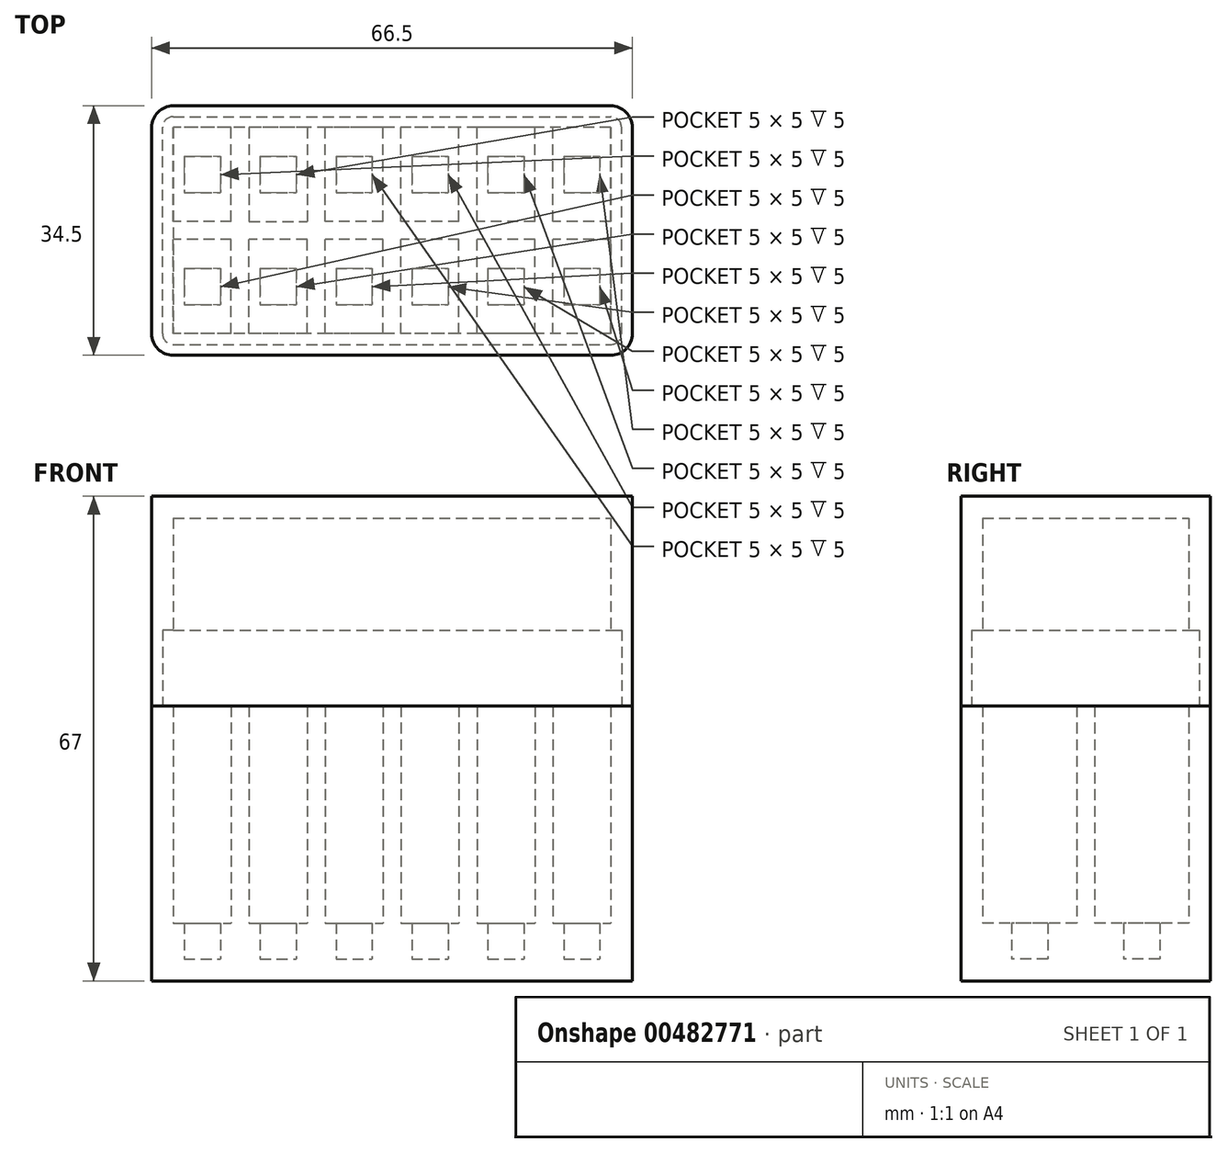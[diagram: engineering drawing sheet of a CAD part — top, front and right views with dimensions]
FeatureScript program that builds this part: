
annotation { "Feature Type Name" : "Feature", "Feature Type Description" : "" }
export const myFeature = defineFeature(function(context is Context, id is Id, definition is map)
    precondition{}
    {
        {
            var Q0;
            Q0=qCreatedBy(makeId("Top.planeOp"),FACE);
            var sketch = newSketch(context, id + "F0", { "sketchPlane" : qUnion([Q0])});
            skLineSegment(sketch, "E0.bottom", {"start": v(3, 0) * mm, "end": v(63.5, 0) * mm});
            skLineSegment(sketch, "E0.top", {"start": v(3, 34.5) * mm, "end": v(63.5, 34.5) * mm});
            skLineSegment(sketch, "E0.left", {"start": v(0, 3) * mm, "end": v(0, 31.5) * mm});
            skLineSegment(sketch, "E0.right", {"start": v(66.5, 3) * mm, "end": v(66.5, 31.5) * mm});
            skPoint(sketch, "E1.visualSharp", {"position": v(0, 34.5) * mm});
            skArc(sketch, "E1.filletArc", {"start": v(3, 34.5) * mm, "mid": v(0.88, 33.62) * mm, "end": v(0, 31.5) * mm});
            skPoint(sketch, "E2.visualSharp", {"position": v(66.5, 34.5) * mm});
            skArc(sketch, "E2.filletArc", {"start": v(66.5, 31.5) * mm, "mid": v(65.62, 33.62) * mm, "end": v(63.5, 34.5) * mm});
            skPoint(sketch, "E3.visualSharp", {"position": v(66.5, 0) * mm});
            skArc(sketch, "E3.filletArc", {"start": v(63.5, 0) * mm, "mid": v(65.62, 0.88) * mm, "end": v(66.5, 3) * mm});
            skPoint(sketch, "E4.visualSharp", {"position": v(0, 0) * mm});
            skArc(sketch, "E4.filletArc", {"start": v(0, 3) * mm, "mid": v(0.88, 0.88) * mm, "end": v(3, 0) * mm});
            skSolve(sketch);
        }
        {
            var Q0;
            Q0 = qSketchRegion(id + "F0", true);
            extrude(context, id + "F1", {"entities" : qUnion([Q0]), "depth" : 3 * mm});
        }
        {
            var Q0;
            Q0=makeQuery(id+"F1.opExtrude","CAP_FACE",FACE,{"disambiguationData":[OSD([sQuery(id+"F0.wireOp",EDGE,"E0.bottom"),sQuery(id+"F0.wireOp",EDGE,"E0.top"),sQuery(id+"F0.wireOp",EDGE,"E0.left"),sQuery(id+"F0.wireOp",EDGE,"E0.right"),sQuery(id+"F0.wireOp",EDGE,"E1.filletArc"),sQuery(id+"F0.wireOp",EDGE,"E2.filletArc"),sQuery(id+"F0.wireOp",EDGE,"E3.filletArc"),sQuery(id+"F0.wireOp",EDGE,"E4.filletArc")])],"isStart":false});
            var sketch = newSketch(context, id + "F2", { "sketchPlane" : qUnion([Q0])});
            skArc(sketch, "E5.0", {"start": v(63.5, 0) * mm, "mid": v(65.62, 0.88) * mm, "end": v(66.5, 3) * mm});
            skLineSegment(sketch, "E5.1", {"start": v(3, 34.5) * mm, "end": v(63.5, 34.5) * mm});
            skArc(sketch, "E5.2", {"start": v(66.5, 31.5) * mm, "mid": v(65.62, 33.62) * mm, "end": v(63.5, 34.5) * mm});
            skLineSegment(sketch, "E5.3", {"start": v(3, 0) * mm, "end": v(63.5, 0) * mm});
            skArc(sketch, "E5.4", {"start": v(3, 34.5) * mm, "mid": v(0.88, 33.62) * mm, "end": v(0, 31.5) * mm});
            skLineSegment(sketch, "E5.5", {"start": v(66.5, 3) * mm, "end": v(66.5, 31.5) * mm});
            skArc(sketch, "E5.6", {"start": v(0, 3) * mm, "mid": v(0.88, 0.88) * mm, "end": v(3, 0) * mm});
            skLineSegment(sketch, "E5.7", {"start": v(0, 3) * mm, "end": v(0, 31.5) * mm});
            skLineSegment(sketch, "E6.bottom", {"start": v(4.5, 12) * mm, "end": v(9.5, 12) * mm});
            skLineSegment(sketch, "E6.top", {"start": v(4.5, 7) * mm, "end": v(9.5, 7) * mm});
            skLineSegment(sketch, "E6.left", {"start": v(4.5, 12) * mm, "end": v(4.5, 7) * mm});
            skLineSegment(sketch, "E6.right", {"start": v(9.5, 12) * mm, "end": v(9.5, 7) * mm});
            skLineSegment(sketch, "E7.0.1.0", {"start": v(4.5, 22.5) * mm, "end": v(9.5, 22.5) * mm});
            skLineSegment(sketch, "E7.0.1.1", {"start": v(9.5, 27.5) * mm, "end": v(9.5, 22.5) * mm});
            skLineSegment(sketch, "E7.0.1.2", {"start": v(4.5, 27.5) * mm, "end": v(4.5, 22.5) * mm});
            skLineSegment(sketch, "E7.0.1.3", {"start": v(4.5, 27.5) * mm, "end": v(9.5, 27.5) * mm});
            skLineSegment(sketch, "E7.1.0.0", {"start": v(15, 7) * mm, "end": v(20, 7) * mm});
            skLineSegment(sketch, "E7.1.0.1", {"start": v(20, 12) * mm, "end": v(20, 7) * mm});
            skLineSegment(sketch, "E7.1.0.2", {"start": v(15, 12) * mm, "end": v(15, 7) * mm});
            skLineSegment(sketch, "E7.1.0.3", {"start": v(15, 12) * mm, "end": v(20, 12) * mm});
            skLineSegment(sketch, "E7.1.1.0", {"start": v(15, 22.5) * mm, "end": v(20, 22.5) * mm});
            skLineSegment(sketch, "E7.1.1.1", {"start": v(20, 27.5) * mm, "end": v(20, 22.5) * mm});
            skLineSegment(sketch, "E7.1.1.2", {"start": v(15, 27.5) * mm, "end": v(15, 22.5) * mm});
            skLineSegment(sketch, "E7.1.1.3", {"start": v(15, 27.5) * mm, "end": v(20, 27.5) * mm});
            skLineSegment(sketch, "E7.2.0.0", {"start": v(25.5, 7) * mm, "end": v(30.5, 7) * mm});
            skLineSegment(sketch, "E7.2.0.1", {"start": v(30.5, 12) * mm, "end": v(30.5, 7) * mm});
            skLineSegment(sketch, "E7.2.0.2", {"start": v(25.5, 12) * mm, "end": v(25.5, 7) * mm});
            skLineSegment(sketch, "E7.2.0.3", {"start": v(25.5, 12) * mm, "end": v(30.5, 12) * mm});
            skLineSegment(sketch, "E7.2.1.0", {"start": v(25.5, 22.5) * mm, "end": v(30.5, 22.5) * mm});
            skLineSegment(sketch, "E7.2.1.1", {"start": v(30.5, 27.5) * mm, "end": v(30.5, 22.5) * mm});
            skLineSegment(sketch, "E7.2.1.2", {"start": v(25.5, 27.5) * mm, "end": v(25.5, 22.5) * mm});
            skLineSegment(sketch, "E7.2.1.3", {"start": v(25.5, 27.5) * mm, "end": v(30.5, 27.5) * mm});
            skLineSegment(sketch, "E7.3.0.0", {"start": v(36, 7) * mm, "end": v(41, 7) * mm});
            skLineSegment(sketch, "E7.3.0.1", {"start": v(41, 12) * mm, "end": v(41, 7) * mm});
            skLineSegment(sketch, "E7.3.0.2", {"start": v(36, 12) * mm, "end": v(36, 7) * mm});
            skLineSegment(sketch, "E7.3.0.3", {"start": v(36, 12) * mm, "end": v(41, 12) * mm});
            skLineSegment(sketch, "E7.3.1.0", {"start": v(36, 22.5) * mm, "end": v(41, 22.5) * mm});
            skLineSegment(sketch, "E7.3.1.1", {"start": v(41, 27.5) * mm, "end": v(41, 22.5) * mm});
            skLineSegment(sketch, "E7.3.1.2", {"start": v(36, 27.5) * mm, "end": v(36, 22.5) * mm});
            skLineSegment(sketch, "E7.3.1.3", {"start": v(36, 27.5) * mm, "end": v(41, 27.5) * mm});
            skLineSegment(sketch, "E7.4.0.0", {"start": v(46.5, 7) * mm, "end": v(51.5, 7) * mm});
            skLineSegment(sketch, "E7.4.0.1", {"start": v(51.5, 12) * mm, "end": v(51.5, 7) * mm});
            skLineSegment(sketch, "E7.4.0.2", {"start": v(46.5, 12) * mm, "end": v(46.5, 7) * mm});
            skLineSegment(sketch, "E7.4.0.3", {"start": v(46.5, 12) * mm, "end": v(51.5, 12) * mm});
            skLineSegment(sketch, "E7.4.1.0", {"start": v(46.5, 22.5) * mm, "end": v(51.5, 22.5) * mm});
            skLineSegment(sketch, "E7.4.1.1", {"start": v(51.5, 27.5) * mm, "end": v(51.5, 22.5) * mm});
            skLineSegment(sketch, "E7.4.1.2", {"start": v(46.5, 27.5) * mm, "end": v(46.5, 22.5) * mm});
            skLineSegment(sketch, "E7.4.1.3", {"start": v(46.5, 27.5) * mm, "end": v(51.5, 27.5) * mm});
            skLineSegment(sketch, "E7.5.0.0", {"start": v(57, 7) * mm, "end": v(62, 7) * mm});
            skLineSegment(sketch, "E7.5.0.1", {"start": v(62, 12) * mm, "end": v(62, 7) * mm});
            skLineSegment(sketch, "E7.5.0.2", {"start": v(57, 12) * mm, "end": v(57, 7) * mm});
            skLineSegment(sketch, "E7.5.0.3", {"start": v(57, 12) * mm, "end": v(62, 12) * mm});
            skLineSegment(sketch, "E7.5.1.0", {"start": v(57, 22.5) * mm, "end": v(62, 22.5) * mm});
            skLineSegment(sketch, "E7.5.1.1", {"start": v(62, 27.5) * mm, "end": v(62, 22.5) * mm});
            skLineSegment(sketch, "E7.5.1.2", {"start": v(57, 27.5) * mm, "end": v(57, 22.5) * mm});
            skLineSegment(sketch, "E7.5.1.3", {"start": v(57, 27.5) * mm, "end": v(62, 27.5) * mm});
            skLineSegment(sketch, "E7.direction1", {"start": v(4.5, 7) * mm, "end": v(15, 7) * mm, "construction": true});
            skLineSegment(sketch, "E7.direction2", {"start": v(4.5, 7) * mm, "end": v(4.5, 22.5) * mm, "construction": true});
            skSolve(sketch);
        }
        {
            var Q0;
            Q0 = qSketchRegion(id + "F2", true);
            extrude(context, id + "F3", {"entities" : qUnion([Q0]), "operationType" : NewBodyOperationType.ADD, "depth" : 5 * mm});
        }
        {
            var Q0;
            Q0=makeQuery(id+"F3.opExtrude","CAP_FACE",FACE,{"disambiguationData":[OSD([sQuery(id+"F2.wireOp",EDGE,"E5.0"),sQuery(id+"F2.wireOp",EDGE,"E5.1"),sQuery(id+"F2.wireOp",EDGE,"E5.2"),sQuery(id+"F2.wireOp",EDGE,"E5.3"),sQuery(id+"F2.wireOp",EDGE,"E5.4"),sQuery(id+"F2.wireOp",EDGE,"E5.5"),sQuery(id+"F2.wireOp",EDGE,"E5.6"),sQuery(id+"F2.wireOp",EDGE,"E5.7"),sQuery(id+"F2.wireOp",EDGE,"E6.bottom"),sQuery(id+"F2.wireOp",EDGE,"E6.top"),sQuery(id+"F2.wireOp",EDGE,"E6.left"),sQuery(id+"F2.wireOp",EDGE,"E6.right"),sQuery(id+"F2.wireOp",EDGE,"E7.0.1.0"),sQuery(id+"F2.wireOp",EDGE,"E7.0.1.1"),sQuery(id+"F2.wireOp",EDGE,"E7.0.1.2"),sQuery(id+"F2.wireOp",EDGE,"E7.0.1.3"),sQuery(id+"F2.wireOp",EDGE,"E7.1.0.0"),sQuery(id+"F2.wireOp",EDGE,"E7.1.0.1"),sQuery(id+"F2.wireOp",EDGE,"E7.1.0.2"),sQuery(id+"F2.wireOp",EDGE,"E7.1.0.3"),sQuery(id+"F2.wireOp",EDGE,"E7.1.1.0"),sQuery(id+"F2.wireOp",EDGE,"E7.1.1.1"),sQuery(id+"F2.wireOp",EDGE,"E7.1.1.2"),sQuery(id+"F2.wireOp",EDGE,"E7.1.1.3"),sQuery(id+"F2.wireOp",EDGE,"E7.2.0.0"),sQuery(id+"F2.wireOp",EDGE,"E7.2.0.1"),sQuery(id+"F2.wireOp",EDGE,"E7.2.0.2"),sQuery(id+"F2.wireOp",EDGE,"E7.2.0.3"),sQuery(id+"F2.wireOp",EDGE,"E7.2.1.0"),sQuery(id+"F2.wireOp",EDGE,"E7.2.1.1"),sQuery(id+"F2.wireOp",EDGE,"E7.2.1.2"),sQuery(id+"F2.wireOp",EDGE,"E7.2.1.3"),sQuery(id+"F2.wireOp",EDGE,"E7.3.0.0"),sQuery(id+"F2.wireOp",EDGE,"E7.3.0.1"),sQuery(id+"F2.wireOp",EDGE,"E7.3.0.2"),sQuery(id+"F2.wireOp",EDGE,"E7.3.0.3"),sQuery(id+"F2.wireOp",EDGE,"E7.3.1.0"),sQuery(id+"F2.wireOp",EDGE,"E7.3.1.1"),sQuery(id+"F2.wireOp",EDGE,"E7.3.1.2"),sQuery(id+"F2.wireOp",EDGE,"E7.3.1.3"),sQuery(id+"F2.wireOp",EDGE,"E7.4.0.0"),sQuery(id+"F2.wireOp",EDGE,"E7.4.0.1"),sQuery(id+"F2.wireOp",EDGE,"E7.4.0.2"),sQuery(id+"F2.wireOp",EDGE,"E7.4.0.3"),sQuery(id+"F2.wireOp",EDGE,"E7.4.1.0"),sQuery(id+"F2.wireOp",EDGE,"E7.4.1.1"),sQuery(id+"F2.wireOp",EDGE,"E7.4.1.2"),sQuery(id+"F2.wireOp",EDGE,"E7.4.1.3"),sQuery(id+"F2.wireOp",EDGE,"E7.5.0.0"),sQuery(id+"F2.wireOp",EDGE,"E7.5.0.1"),sQuery(id+"F2.wireOp",EDGE,"E7.5.0.2"),sQuery(id+"F2.wireOp",EDGE,"E7.5.0.3"),sQuery(id+"F2.wireOp",EDGE,"E7.5.1.0"),sQuery(id+"F2.wireOp",EDGE,"E7.5.1.1"),sQuery(id+"F2.wireOp",EDGE,"E7.5.1.2"),sQuery(id+"F2.wireOp",EDGE,"E7.5.1.3")])],"isStart":false});
            var sketch = newSketch(context, id + "F4", { "sketchPlane" : qUnion([Q0])});
            skLineSegment(sketch, "E8.bottom", {"start": v(3, 16) * mm, "end": v(11, 16) * mm});
            skLineSegment(sketch, "E8.top", {"start": v(3, 3) * mm, "end": v(11, 3) * mm});
            skLineSegment(sketch, "E8.left", {"start": v(3, 16) * mm, "end": v(3, 3) * mm});
            skLineSegment(sketch, "E8.right", {"start": v(11, 16) * mm, "end": v(11, 3) * mm});
            skLineSegment(sketch, "E9.0.1.0", {"start": v(3, 18.5) * mm, "end": v(11, 18.5) * mm});
            skLineSegment(sketch, "E9.0.1.1", {"start": v(3, 31.5) * mm, "end": v(11, 31.5) * mm});
            skLineSegment(sketch, "E9.0.1.2", {"start": v(11, 31.5) * mm, "end": v(11, 18.5) * mm});
            skLineSegment(sketch, "E9.0.1.3", {"start": v(3, 31.5) * mm, "end": v(3, 18.5) * mm});
            skLineSegment(sketch, "E9.1.0.0", {"start": v(13.5, 3) * mm, "end": v(21.5, 3) * mm});
            skLineSegment(sketch, "E9.1.0.1", {"start": v(13.5, 16) * mm, "end": v(21.5, 16) * mm});
            skLineSegment(sketch, "E9.1.0.2", {"start": v(21.5, 16) * mm, "end": v(21.5, 3) * mm});
            skLineSegment(sketch, "E9.1.0.3", {"start": v(13.5, 16) * mm, "end": v(13.5, 3) * mm});
            skLineSegment(sketch, "E9.1.1.0", {"start": v(13.5, 18.5) * mm, "end": v(21.5, 18.5) * mm});
            skLineSegment(sketch, "E9.1.1.1", {"start": v(13.5, 31.5) * mm, "end": v(21.5, 31.5) * mm});
            skLineSegment(sketch, "E9.1.1.2", {"start": v(21.5, 31.5) * mm, "end": v(21.5, 18.5) * mm});
            skLineSegment(sketch, "E9.1.1.3", {"start": v(13.5, 31.5) * mm, "end": v(13.5, 18.5) * mm});
            skLineSegment(sketch, "E9.2.0.0", {"start": v(24, 3) * mm, "end": v(32, 3) * mm});
            skLineSegment(sketch, "E9.2.0.1", {"start": v(24, 16) * mm, "end": v(32, 16) * mm});
            skLineSegment(sketch, "E9.2.0.2", {"start": v(32, 16) * mm, "end": v(32, 3) * mm});
            skLineSegment(sketch, "E9.2.0.3", {"start": v(24, 16) * mm, "end": v(24, 3) * mm});
            skLineSegment(sketch, "E9.2.1.0", {"start": v(24, 18.5) * mm, "end": v(32, 18.5) * mm});
            skLineSegment(sketch, "E9.2.1.1", {"start": v(24, 31.5) * mm, "end": v(32, 31.5) * mm});
            skLineSegment(sketch, "E9.2.1.2", {"start": v(32, 31.5) * mm, "end": v(32, 18.5) * mm});
            skLineSegment(sketch, "E9.2.1.3", {"start": v(24, 31.5) * mm, "end": v(24, 18.5) * mm});
            skLineSegment(sketch, "E9.3.0.0", {"start": v(34.5, 3) * mm, "end": v(42.5, 3) * mm});
            skLineSegment(sketch, "E9.3.0.1", {"start": v(34.5, 16) * mm, "end": v(42.5, 16) * mm});
            skLineSegment(sketch, "E9.3.0.2", {"start": v(42.5, 16) * mm, "end": v(42.5, 3) * mm});
            skLineSegment(sketch, "E9.3.0.3", {"start": v(34.5, 16) * mm, "end": v(34.5, 3) * mm});
            skLineSegment(sketch, "E9.3.1.0", {"start": v(34.5, 18.5) * mm, "end": v(42.5, 18.5) * mm});
            skLineSegment(sketch, "E9.3.1.1", {"start": v(34.5, 31.5) * mm, "end": v(42.5, 31.5) * mm});
            skLineSegment(sketch, "E9.3.1.2", {"start": v(42.5, 31.5) * mm, "end": v(42.5, 18.5) * mm});
            skLineSegment(sketch, "E9.3.1.3", {"start": v(34.5, 31.5) * mm, "end": v(34.5, 18.5) * mm});
            skLineSegment(sketch, "E9.4.0.0", {"start": v(45, 3) * mm, "end": v(53, 3) * mm});
            skLineSegment(sketch, "E9.4.0.1", {"start": v(45, 16) * mm, "end": v(53, 16) * mm});
            skLineSegment(sketch, "E9.4.0.2", {"start": v(53, 16) * mm, "end": v(53, 3) * mm});
            skLineSegment(sketch, "E9.4.0.3", {"start": v(45, 16) * mm, "end": v(45, 3) * mm});
            skLineSegment(sketch, "E9.4.1.0", {"start": v(45, 18.5) * mm, "end": v(53, 18.5) * mm});
            skLineSegment(sketch, "E9.4.1.1", {"start": v(45, 31.5) * mm, "end": v(53, 31.5) * mm});
            skLineSegment(sketch, "E9.4.1.2", {"start": v(53, 31.5) * mm, "end": v(53, 18.5) * mm});
            skLineSegment(sketch, "E9.4.1.3", {"start": v(45, 31.5) * mm, "end": v(45, 18.5) * mm});
            skLineSegment(sketch, "E9.5.0.0", {"start": v(55.5, 3) * mm, "end": v(63.5, 3) * mm});
            skLineSegment(sketch, "E9.5.0.1", {"start": v(55.5, 16) * mm, "end": v(63.5, 16) * mm});
            skLineSegment(sketch, "E9.5.0.2", {"start": v(63.5, 16) * mm, "end": v(63.5, 3) * mm});
            skLineSegment(sketch, "E9.5.0.3", {"start": v(55.5, 16) * mm, "end": v(55.5, 3) * mm});
            skLineSegment(sketch, "E9.5.1.0", {"start": v(55.5, 18.5) * mm, "end": v(63.5, 18.5) * mm});
            skLineSegment(sketch, "E9.5.1.1", {"start": v(55.5, 31.5) * mm, "end": v(63.5, 31.5) * mm});
            skLineSegment(sketch, "E9.5.1.2", {"start": v(63.5, 31.5) * mm, "end": v(63.5, 18.5) * mm});
            skLineSegment(sketch, "E9.5.1.3", {"start": v(55.5, 31.5) * mm, "end": v(55.5, 18.5) * mm});
            skLineSegment(sketch, "E9.direction1", {"start": v(3, 3) * mm, "end": v(13.5, 3) * mm, "construction": true});
            skLineSegment(sketch, "E9.direction2", {"start": v(3, 3) * mm, "end": v(3, 18.5) * mm, "construction": true});
            skArc(sketch, "E10.0", {"start": v(63.5, 0) * mm, "mid": v(65.62, 0.88) * mm, "end": v(66.5, 3) * mm});
            skLineSegment(sketch, "E10.1", {"start": v(3, 34.5) * mm, "end": v(63.5, 34.5) * mm});
            skArc(sketch, "E10.2", {"start": v(66.5, 31.5) * mm, "mid": v(65.62, 33.62) * mm, "end": v(63.5, 34.5) * mm});
            skLineSegment(sketch, "E10.3", {"start": v(3, 0) * mm, "end": v(63.5, 0) * mm});
            skArc(sketch, "E10.4", {"start": v(3, 34.5) * mm, "mid": v(0.88, 33.62) * mm, "end": v(0, 31.5) * mm});
            skLineSegment(sketch, "E10.5", {"start": v(66.5, 3) * mm, "end": v(66.5, 31.5) * mm});
            skLineSegment(sketch, "E10.6", {"start": v(0, 3) * mm, "end": v(0, 31.5) * mm});
            skArc(sketch, "E10.7", {"start": v(0, 3) * mm, "mid": v(0.88, 0.88) * mm, "end": v(3, 0) * mm});
            skSolve(sketch);
        }
        {
            var Q0;
            Q0 = qSketchRegion(id + "F4", true);
            extrude(context, id + "F5", {"entities" : qUnion([Q0]), "operationType" : NewBodyOperationType.ADD, "depth" : 40 * mm, "offsetDistance" : 25 * mm});
        }
        {
            var Q0;
            Q0=makeQuery(id+"F5.opExtrude","CAP_FACE",FACE,{"disambiguationData":[OSD([sQuery(id+"F4.wireOp",EDGE,"E8.bottom"),sQuery(id+"F4.wireOp",EDGE,"E8.top"),sQuery(id+"F4.wireOp",EDGE,"E8.left"),sQuery(id+"F4.wireOp",EDGE,"E8.right"),sQuery(id+"F4.wireOp",EDGE,"E9.0.1.0"),sQuery(id+"F4.wireOp",EDGE,"E9.0.1.1"),sQuery(id+"F4.wireOp",EDGE,"E9.0.1.2"),sQuery(id+"F4.wireOp",EDGE,"E9.0.1.3"),sQuery(id+"F4.wireOp",EDGE,"E9.1.0.0"),sQuery(id+"F4.wireOp",EDGE,"E9.1.0.1"),sQuery(id+"F4.wireOp",EDGE,"E9.1.0.2"),sQuery(id+"F4.wireOp",EDGE,"E9.1.0.3"),sQuery(id+"F4.wireOp",EDGE,"E9.1.1.0"),sQuery(id+"F4.wireOp",EDGE,"E9.1.1.1"),sQuery(id+"F4.wireOp",EDGE,"E9.1.1.2"),sQuery(id+"F4.wireOp",EDGE,"E9.1.1.3"),sQuery(id+"F4.wireOp",EDGE,"E9.2.0.0"),sQuery(id+"F4.wireOp",EDGE,"E9.2.0.1"),sQuery(id+"F4.wireOp",EDGE,"E9.2.0.2"),sQuery(id+"F4.wireOp",EDGE,"E9.2.0.3"),sQuery(id+"F4.wireOp",EDGE,"E9.2.1.0"),sQuery(id+"F4.wireOp",EDGE,"E9.2.1.1"),sQuery(id+"F4.wireOp",EDGE,"E9.2.1.2"),sQuery(id+"F4.wireOp",EDGE,"E9.2.1.3"),sQuery(id+"F4.wireOp",EDGE,"E9.3.0.0"),sQuery(id+"F4.wireOp",EDGE,"E9.3.0.1"),sQuery(id+"F4.wireOp",EDGE,"E9.3.0.2"),sQuery(id+"F4.wireOp",EDGE,"E9.3.0.3"),sQuery(id+"F4.wireOp",EDGE,"E9.3.1.0"),sQuery(id+"F4.wireOp",EDGE,"E9.3.1.1"),sQuery(id+"F4.wireOp",EDGE,"E9.3.1.2"),sQuery(id+"F4.wireOp",EDGE,"E9.3.1.3"),sQuery(id+"F4.wireOp",EDGE,"E9.4.0.0"),sQuery(id+"F4.wireOp",EDGE,"E9.4.0.1"),sQuery(id+"F4.wireOp",EDGE,"E9.4.0.2"),sQuery(id+"F4.wireOp",EDGE,"E9.4.0.3"),sQuery(id+"F4.wireOp",EDGE,"E9.4.1.0"),sQuery(id+"F4.wireOp",EDGE,"E9.4.1.1"),sQuery(id+"F4.wireOp",EDGE,"E9.4.1.2"),sQuery(id+"F4.wireOp",EDGE,"E9.4.1.3"),sQuery(id+"F4.wireOp",EDGE,"E9.5.0.0"),sQuery(id+"F4.wireOp",EDGE,"E9.5.0.1"),sQuery(id+"F4.wireOp",EDGE,"E9.5.0.2"),sQuery(id+"F4.wireOp",EDGE,"E9.5.0.3"),sQuery(id+"F4.wireOp",EDGE,"E9.5.1.0"),sQuery(id+"F4.wireOp",EDGE,"E9.5.1.1"),sQuery(id+"F4.wireOp",EDGE,"E9.5.1.2"),sQuery(id+"F4.wireOp",EDGE,"E9.5.1.3"),sQuery(id+"F4.wireOp",EDGE,"E10.0"),sQuery(id+"F4.wireOp",EDGE,"E10.1"),sQuery(id+"F4.wireOp",EDGE,"E10.2"),sQuery(id+"F4.wireOp",EDGE,"E10.3"),sQuery(id+"F4.wireOp",EDGE,"E10.4"),sQuery(id+"F4.wireOp",EDGE,"E10.5"),sQuery(id+"F4.wireOp",EDGE,"E10.6"),sQuery(id+"F4.wireOp",EDGE,"E10.7")])],"isStart":false});
            var sketch = newSketch(context, id + "F6", { "sketchPlane" : qUnion([Q0])});
            skArc(sketch, "E11.0", {"start": v(3, 32.9) * mm, "mid": v(2.01, 32.49) * mm, "end": v(1.6, 31.5) * mm});
            skLineSegment(sketch, "E11.1", {"start": v(1.6, 3) * mm, "end": v(1.6, 31.5) * mm});
            skLineSegment(sketch, "E11.2", {"start": v(3, 32.9) * mm, "end": v(63.5, 32.9) * mm});
            skArc(sketch, "E11.3", {"start": v(1.6, 3) * mm, "mid": v(2.01, 2.01) * mm, "end": v(3, 1.6) * mm});
            skArc(sketch, "E11.4", {"start": v(64.9, 31.5) * mm, "mid": v(64.49, 32.49) * mm, "end": v(63.5, 32.9) * mm});
            skLineSegment(sketch, "E11.5", {"start": v(64.9, 3) * mm, "end": v(64.9, 31.5) * mm});
            skArc(sketch, "E11.6", {"start": v(63.5, 1.6) * mm, "mid": v(64.49, 2.01) * mm, "end": v(64.9, 3) * mm});
            skLineSegment(sketch, "E11.7", {"start": v(3, 1.6) * mm, "end": v(63.5, 1.6) * mm});
            skLineSegment(sketch, "E12.0", {"start": v(3, 34.5) * mm, "end": v(63.5, 34.5) * mm});
            skLineSegment(sketch, "E12.1", {"start": v(0, 3) * mm, "end": v(0, 31.5) * mm});
            skArc(sketch, "E12.2", {"start": v(0, 3) * mm, "mid": v(0.88, 0.88) * mm, "end": v(3, 0) * mm});
            skArc(sketch, "E12.3", {"start": v(63.5, 0) * mm, "mid": v(65.62, 0.88) * mm, "end": v(66.5, 3) * mm});
            skLineSegment(sketch, "E12.4", {"start": v(66.5, 3) * mm, "end": v(66.5, 31.5) * mm});
            skLineSegment(sketch, "E12.5", {"start": v(3, 0) * mm, "end": v(63.5, 0) * mm});
            skArc(sketch, "E12.6", {"start": v(3, 34.5) * mm, "mid": v(0.88, 33.62) * mm, "end": v(0, 31.5) * mm});
            skArc(sketch, "E12.7", {"start": v(66.5, 31.5) * mm, "mid": v(65.62, 33.62) * mm, "end": v(63.5, 34.5) * mm});
            skSolve(sketch);
        }
        {
            var Q0;
            Q0 = qSketchRegion(id + "F6", true);
            extrude(context, id + "F7", {"entities" : qUnion([Q0]), "operationType" : NewBodyOperationType.REMOVE, "oppositeDirection" : true, "depth" : 10 * mm, "offsetDistance" : 25 * mm});
        }
        {
            var Q0;
            Q0=makeQuery(id+"F5.opExtrude","CAP_FACE",FACE,{"disambiguationData":[OSD([sQuery(id+"F4.wireOp",EDGE,"E8.bottom"),sQuery(id+"F4.wireOp",EDGE,"E8.top"),sQuery(id+"F4.wireOp",EDGE,"E8.left"),sQuery(id+"F4.wireOp",EDGE,"E8.right"),sQuery(id+"F4.wireOp",EDGE,"E9.0.1.0"),sQuery(id+"F4.wireOp",EDGE,"E9.0.1.1"),sQuery(id+"F4.wireOp",EDGE,"E9.0.1.2"),sQuery(id+"F4.wireOp",EDGE,"E9.0.1.3"),sQuery(id+"F4.wireOp",EDGE,"E9.1.0.0"),sQuery(id+"F4.wireOp",EDGE,"E9.1.0.1"),sQuery(id+"F4.wireOp",EDGE,"E9.1.0.2"),sQuery(id+"F4.wireOp",EDGE,"E9.1.0.3"),sQuery(id+"F4.wireOp",EDGE,"E9.1.1.0"),sQuery(id+"F4.wireOp",EDGE,"E9.1.1.1"),sQuery(id+"F4.wireOp",EDGE,"E9.1.1.2"),sQuery(id+"F4.wireOp",EDGE,"E9.1.1.3"),sQuery(id+"F4.wireOp",EDGE,"E9.2.0.0"),sQuery(id+"F4.wireOp",EDGE,"E9.2.0.1"),sQuery(id+"F4.wireOp",EDGE,"E9.2.0.2"),sQuery(id+"F4.wireOp",EDGE,"E9.2.0.3"),sQuery(id+"F4.wireOp",EDGE,"E9.2.1.0"),sQuery(id+"F4.wireOp",EDGE,"E9.2.1.1"),sQuery(id+"F4.wireOp",EDGE,"E9.2.1.2"),sQuery(id+"F4.wireOp",EDGE,"E9.2.1.3"),sQuery(id+"F4.wireOp",EDGE,"E9.3.0.0"),sQuery(id+"F4.wireOp",EDGE,"E9.3.0.1"),sQuery(id+"F4.wireOp",EDGE,"E9.3.0.2"),sQuery(id+"F4.wireOp",EDGE,"E9.3.0.3"),sQuery(id+"F4.wireOp",EDGE,"E9.3.1.0"),sQuery(id+"F4.wireOp",EDGE,"E9.3.1.1"),sQuery(id+"F4.wireOp",EDGE,"E9.3.1.2"),sQuery(id+"F4.wireOp",EDGE,"E9.3.1.3"),sQuery(id+"F4.wireOp",EDGE,"E9.4.0.0"),sQuery(id+"F4.wireOp",EDGE,"E9.4.0.1"),sQuery(id+"F4.wireOp",EDGE,"E9.4.0.2"),sQuery(id+"F4.wireOp",EDGE,"E9.4.0.3"),sQuery(id+"F4.wireOp",EDGE,"E9.4.1.0"),sQuery(id+"F4.wireOp",EDGE,"E9.4.1.1"),sQuery(id+"F4.wireOp",EDGE,"E9.4.1.2"),sQuery(id+"F4.wireOp",EDGE,"E9.4.1.3"),sQuery(id+"F4.wireOp",EDGE,"E9.5.0.0"),sQuery(id+"F4.wireOp",EDGE,"E9.5.0.1"),sQuery(id+"F4.wireOp",EDGE,"E9.5.0.2"),sQuery(id+"F4.wireOp",EDGE,"E9.5.0.3"),sQuery(id+"F4.wireOp",EDGE,"E9.5.1.0"),sQuery(id+"F4.wireOp",EDGE,"E9.5.1.1"),sQuery(id+"F4.wireOp",EDGE,"E9.5.1.2"),sQuery(id+"F4.wireOp",EDGE,"E9.5.1.3"),sQuery(id+"F4.wireOp",EDGE,"E10.0"),sQuery(id+"F4.wireOp",EDGE,"E10.1"),sQuery(id+"F4.wireOp",EDGE,"E10.2"),sQuery(id+"F4.wireOp",EDGE,"E10.3"),sQuery(id+"F4.wireOp",EDGE,"E10.4"),sQuery(id+"F4.wireOp",EDGE,"E10.5"),sQuery(id+"F4.wireOp",EDGE,"E10.6"),sQuery(id+"F4.wireOp",EDGE,"E10.7")])],"isStart":false});
            var sketch = newSketch(context, id + "F8", { "sketchPlane" : qUnion([Q0])});
            skLineSegment(sketch, "E13.0", {"start": v(3, 0) * mm, "end": v(63.5, 0) * mm});
            skLineSegment(sketch, "E13.1", {"start": v(3, 34.5) * mm, "end": v(63.5, 34.5) * mm});
            skLineSegment(sketch, "E13.2", {"start": v(0, 3) * mm, "end": v(0, 31.5) * mm});
            skLineSegment(sketch, "E13.3", {"start": v(66.5, 3) * mm, "end": v(66.5, 31.5) * mm});
            skPoint(sketch, "E13.4", {"position": v(0, 34.5) * mm});
            skArc(sketch, "E13.5", {"start": v(3, 34.5) * mm, "mid": v(0.88, 33.62) * mm, "end": v(0, 31.5) * mm});
            skPoint(sketch, "E13.6", {"position": v(66.5, 34.5) * mm});
            skArc(sketch, "E13.7", {"start": v(66.5, 31.5) * mm, "mid": v(65.62, 33.62) * mm, "end": v(63.5, 34.5) * mm});
            skPoint(sketch, "E13.8", {"position": v(66.5, 0) * mm});
            skArc(sketch, "E13.9", {"start": v(63.5, 0) * mm, "mid": v(65.62, 0.88) * mm, "end": v(66.5, 3) * mm});
            skPoint(sketch, "E13.10", {"position": v(0, 0) * mm});
            skArc(sketch, "E13.11", {"start": v(0, 3) * mm, "mid": v(0.88, 0.88) * mm, "end": v(3, 0) * mm});
            skSolve(sketch);
        }
        {
            var Q0;
            Q0 = qSketchRegion(id + "F8", true);
            extrude(context, id + "F9", {"entities" : qUnion([Q0]), "depth" : 19 * mm, "offsetDistance" : 25 * mm, "hasSecondDirection" : true, "secondDirectionOppositeDirection" : true, "secondDirectionDepth" : 10 * mm});
        }
        {
            var Q0;
            Q0=makeQuery(id+"F9.opExtrude","CAP_FACE",FACE,{"disambiguationData":[OSD([sQuery(id+"F8.wireOp",EDGE,"E13.0"),sQuery(id+"F8.wireOp",EDGE,"E13.1"),sQuery(id+"F8.wireOp",EDGE,"E13.2"),sQuery(id+"F8.wireOp",EDGE,"E13.3"),sQuery(id+"F8.wireOp",EDGE,"E13.5"),sQuery(id+"F8.wireOp",EDGE,"E13.7"),sQuery(id+"F8.wireOp",EDGE,"E13.9"),sQuery(id+"F8.wireOp",EDGE,"E13.11")])],"isStart":true});
            var sketch = newSketch(context, id + "F10", { "sketchPlane" : qUnion([Q0])});
            skLineSegment(sketch, "E14.0", {"start": v(3, -3) * mm, "end": v(3, -31.5) * mm});
            skLineSegment(sketch, "E14.1", {"start": v(3, -3) * mm, "end": v(63.5, -3) * mm});
            skLineSegment(sketch, "E14.2", {"start": v(63.5, -3) * mm, "end": v(63.5, -31.5) * mm});
            skLineSegment(sketch, "E14.3", {"start": v(3, -31.5) * mm, "end": v(63.5, -31.5) * mm});
            skSolve(sketch);
        }
        {
            var Q0;
            Q0 = qSketchRegion(id + "F10", true);
            extrude(context, id + "F11", {"entities" : qUnion([Q0]), "operationType" : NewBodyOperationType.REMOVE, "oppositeDirection" : true, "depth" : 26 * mm, "offsetDistance" : 25 * mm});
        }
        {
            var Q0;
            Q0=makeQuery(id+"F9.opExtrude","CAP_FACE",FACE,{"disambiguationData":[OSD([sQuery(id+"F8.wireOp",EDGE,"E13.0"),sQuery(id+"F8.wireOp",EDGE,"E13.1"),sQuery(id+"F8.wireOp",EDGE,"E13.2"),sQuery(id+"F8.wireOp",EDGE,"E13.3"),sQuery(id+"F8.wireOp",EDGE,"E13.5"),sQuery(id+"F8.wireOp",EDGE,"E13.7"),sQuery(id+"F8.wireOp",EDGE,"E13.9"),sQuery(id+"F8.wireOp",EDGE,"E13.11")])],"isStart":true});
            var sketch = newSketch(context, id + "F12", { "sketchPlane" : qUnion([Q0])});
            skArc(sketch, "E15.0", {"start": v(1.5, -3) * mm, "mid": v(1.94, -1.94) * mm, "end": v(3, -1.5) * mm});
            skLineSegment(sketch, "E15.1", {"start": v(1.5, -3) * mm, "end": v(1.5, -31.5) * mm});
            skLineSegment(sketch, "E15.2", {"start": v(3, -1.5) * mm, "end": v(63.5, -1.5) * mm});
            skArc(sketch, "E15.3", {"start": v(3, -33) * mm, "mid": v(1.94, -32.56) * mm, "end": v(1.5, -31.5) * mm});
            skArc(sketch, "E15.4", {"start": v(63.5, -1.5) * mm, "mid": v(64.56, -1.94) * mm, "end": v(65, -3) * mm});
            skLineSegment(sketch, "E15.5", {"start": v(65, -3) * mm, "end": v(65, -31.5) * mm});
            skArc(sketch, "E15.6", {"start": v(65, -31.5) * mm, "mid": v(64.56, -32.56) * mm, "end": v(63.5, -33) * mm});
            skLineSegment(sketch, "E15.7", {"start": v(3, -33) * mm, "end": v(63.5, -33) * mm});
            skSolve(sketch);
        }
        {
            var Q0;
            Q0 = qSketchRegion(id + "F12", true);
            extrude(context, id + "F13", {"entities" : qUnion([Q0]), "operationType" : NewBodyOperationType.REMOVE, "oppositeDirection" : true, "depth" : 10.5 * mm, "offsetDistance" : 25 * mm});
        }
    });
